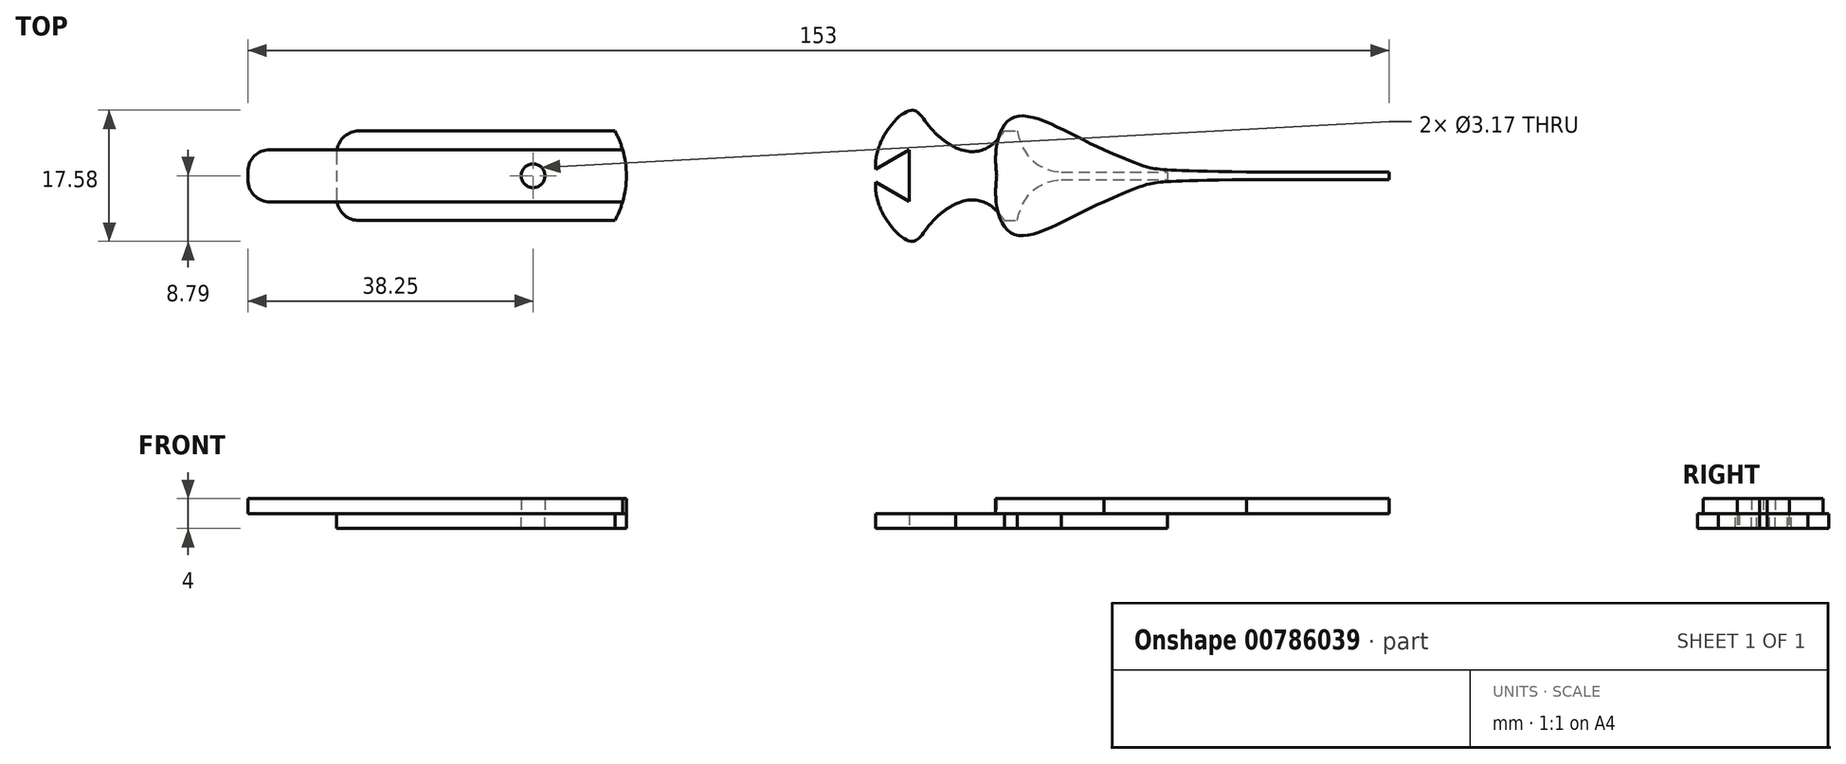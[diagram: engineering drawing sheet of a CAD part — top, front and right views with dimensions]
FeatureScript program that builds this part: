
annotation { "Feature Type Name" : "Feature", "Feature Type Description" : "" }
export const myFeature = defineFeature(function(context is Context, id is Id, definition is map)
    precondition{}
    {
        {
            var Q0;
            Q0=qCreatedBy(makeId("Top.planeOp"),FACE);
            var sketch = newSketch(context, id + "F0", { "sketchPlane" : qUnion([Q0])});
            skCircle(sketch, "E0", {"center": v(0, 0) * mm, "radius": 1.59 * mm});
            skLineSegment(sketch, "E1.bottom", {"start": v(-38.25, 3.5) * mm, "end": v(114.75, 3.5) * mm});
            skLineSegment(sketch, "E1.top", {"start": v(-38.25, -3.5) * mm, "end": v(114.75, -3.5) * mm});
            skLineSegment(sketch, "E1.left", {"start": v(-38.25, 3.5) * mm, "end": v(-38.25, -3.5) * mm});
            skLineSegment(sketch, "E1.right", {"start": v(114.75, 3.5) * mm, "end": v(114.75, -3.5) * mm});
            skCircle(sketch, "E2", {"center": v(0, 0) * mm, "radius": 12.5 * mm});
            skFitSpline(sketch, "E3", {"points": [v(76.5, -3.5) * mm, v(83.35, -0.96) * mm, v(95.63, -0.5) * mm], "startDerivative": vector(32.58, 14.52) * mm, "endDerivative": vector(48.68, 0.82) * mm});
            skFitSpline(sketch, "E4", {"points": [v(76.5, -3.5) * mm, v(64.47, -7.85) * mm, v(62.16, 0) * mm], "startDerivative": vector(-24.35, -10.45) * mm, "endDerivative": vector(3.38, 23.63) * mm});
            skLineSegment(sketch, "E5", {"start": v(0, 0) * mm, "end": v(229.5, 0) * mm, "construction": true});
            skLineSegment(sketch, "E6", {"start": v(95.63, -0.5) * mm, "end": v(114.75, -0.5) * mm});
            skFitSpline(sketch, "E7.MirrorCS", {"points": [v(76.5, 3.5) * mm, v(64.47, 7.85) * mm, v(62.16, 0) * mm], "startDerivative": vector(-24.35, 10.45) * mm, "endDerivative": vector(3.38, -23.63) * mm});
            skFitSpline(sketch, "E8.MirrorCS", {"points": [v(76.5, 3.5) * mm, v(83.35, 0.96) * mm, v(95.63, 0.5) * mm], "startDerivative": vector(32.58, -14.52) * mm, "endDerivative": vector(48.68, -0.82) * mm});
            skLineSegment(sketch, "E9.MirrorCS", {"start": v(95.63, 0.5) * mm, "end": v(114.75, 0.5) * mm});
            skSolve(sketch);
        }
        {
            var Q0;
            {var subQ0=sQuery(id+"F0.wireOp",EDGE,"E1.left");Q0=makeQuery(id+"F0.imprint","IMPRINT",FACE,{"disambiguationData":[TD([[makeQuery(id+"F0.imprint","IMPRINT",EDGE,{"derivedFrom":subQ0}),1.0]])]});}
            var Q1;
            {var subQ0=sQuery(id+"F0.wireOp",EDGE,"E2");var subQ1=sQuery(id+"F0.wireOp",EDGE,"E1.bottom");var subQ2=makeQuery(id+"F0.imprint","INTERSECT",VERTEX,{"disambiguationData":[OD(0.0)],"derivedFrom":[subQ1,subQ0]});Q1=makeQuery(id+"F0.imprint","IMPRINT",FACE,{"disambiguationData":[TD([[makeQuery(id+"F0.imprint","IMPRINT",EDGE,{"disambiguationData":[TD([[subQ2,-1.0]])],"derivedFrom":subQ1}),1.0]])]});}
            var Q2;
            {var subQ0=sQuery(id+"F0.wireOp",EDGE,"E7.MirrorCS");var subQ1=sQuery(id+"F0.wireOp",EDGE,"E1.bottom");var subQ3=makeQuery(id+"F0.imprint","INTERSECT",VERTEX,{"derivedFrom":[subQ1,subQ0]});Q2=makeQuery(id+"F0.imprint","IMPRINT",FACE,{"disambiguationData":[TD([[makeQuery(id+"F0.imprint","IMPRINT",EDGE,{"disambiguationData":[TD([[subQ3,-1.0]])],"derivedFrom":subQ1}),1.0]])]});}
            var Q3;
            {var subQ0=sQuery(id+"F0.wireOp",EDGE,"E2");var subQ1=sQuery(id+"F0.wireOp",EDGE,"E1.top");var subQ2=makeQuery(id+"F0.imprint","INTERSECT",VERTEX,{"disambiguationData":[OD(0.0)],"derivedFrom":[subQ1,subQ0]});Q3=makeQuery(id+"F0.imprint","IMPRINT",FACE,{"disambiguationData":[TD([[makeQuery(id+"F0.imprint","IMPRINT",EDGE,{"disambiguationData":[TD([[subQ2,-1.0]])],"derivedFrom":subQ1}),-1.0]])]});}
            var Q4;
            {var subQ0=sQuery(id+"F0.wireOp",EDGE,"E4");var subQ1=sQuery(id+"F0.wireOp",EDGE,"E1.top");var subQ3=makeQuery(id+"F0.imprint","INTERSECT",VERTEX,{"derivedFrom":[subQ1,subQ0]});Q4=makeQuery(id+"F0.imprint","IMPRINT",FACE,{"disambiguationData":[TD([[makeQuery(id+"F0.imprint","IMPRINT",EDGE,{"disambiguationData":[TD([[subQ3,-1.0]])],"derivedFrom":subQ1}),-1.0]])]});}
            var Q5;
            {var subQ5=sQuery(id+"F0.wireOp",EDGE,"E2");var subQ6=sQuery(id+"F0.wireOp",EDGE,"E1.bottom");var subQ7=makeQuery(id+"F0.imprint","INTERSECT",VERTEX,{"disambiguationData":[OD(1.0)],"derivedFrom":[subQ6,subQ5]});Q5=makeQuery(id+"F0.imprint","IMPRINT",FACE,{"disambiguationData":[TD([[makeQuery(id+"F0.imprint","IMPRINT",EDGE,{"disambiguationData":[TD([[subQ7,-1.0]])],"derivedFrom":subQ6}),-1.0]])]});}
            var Q6;
            Q6=makeQuery(id+"F0.imprint","IMPRINT",FACE,{"disambiguationData":[TD([[makeQuery(id+"F0.imprint","IMPRINT",EDGE,{"derivedFrom":sQuery(id+"F0.wireOp",EDGE,"E0")}),-1.0]])]});
            var Q7;
            {var subQ8=sQuery(id+"F0.wireOp",EDGE,"E3");Q7=makeQuery(id+"F0.imprint","IMPRINT",FACE,{"disambiguationData":[TD([[makeQuery(id+"F0.imprint","IMPRINT",EDGE,{"derivedFrom":subQ8}),1.0]])]});}
            extrude(context, id + "F1", {"entities" : qUnion([Q0, Q1, Q2, Q3, Q4, Q5, Q6, Q7]), "depth" : 2 * mm});
        }
        {
            var Q0;
            Q0=qCreatedBy(makeId("Top.planeOp"),FACE);
            var sketch = newSketch(context, id + "F2", { "sketchPlane" : qUnion([Q0])});
            skCircle(sketch, "E10", {"center": v(0, 0) * mm, "radius": 1.59 * mm});
            skLineSegment(sketch, "E11.bottom", {"start": v(-26.33, 6) * mm, "end": v(85, 6) * mm});
            skLineSegment(sketch, "E11.top", {"start": v(-26.33, -6) * mm, "end": v(85, -6) * mm});
            skLineSegment(sketch, "E11.left", {"start": v(-26.33, 6) * mm, "end": v(-26.33, -6) * mm});
            skLineSegment(sketch, "E11.right", {"start": v(85, 6) * mm, "end": v(85, -6) * mm});
            skCircle(sketch, "E12", {"center": v(0, 0) * mm, "radius": 12.5 * mm});
            skLineSegment(sketch, "E13.right", {"start": v(85, -12.54) * mm, "end": v(85, -19.22) * mm});
            skFitSpline(sketch, "E14", {"points": [v(56.67, -3.75) * mm, v(64.42, -7.88) * mm, v(70.83, -0.5) * mm], "startDerivative": vector(32.58, 14.52) * mm, "endDerivative": vector(38.81, 3.07) * mm});
            skFitSpline(sketch, "E15", {"points": [v(56.67, -3.75) * mm, v(50.67, -8.78) * mm, v(46.04, 0) * mm], "startDerivative": vector(-26.59, -13.5) * mm, "endDerivative": vector(5.2, 23.3) * mm});
            skLineSegment(sketch, "E16", {"start": v(0, 0) * mm, "end": v(229.5, 0) * mm, "construction": true});
            skLineSegment(sketch, "E17", {"start": v(70.83, -0.5) * mm, "end": v(85, -0.5) * mm});
            skFitSpline(sketch, "E18.MirrorCS", {"points": [v(56.67, 3.75) * mm, v(50.67, 8.78) * mm, v(46.04, 0) * mm], "startDerivative": vector(-26.59, 13.5) * mm, "endDerivative": vector(5.2, -23.3) * mm});
            skFitSpline(sketch, "E19.MirrorCS", {"points": [v(56.67, 3.75) * mm, v(64.42, 7.88) * mm, v(70.83, 0.5) * mm], "startDerivative": vector(32.58, -14.52) * mm, "endDerivative": vector(38.81, -3.07) * mm});
            skLineSegment(sketch, "E20.MirrorCS", {"start": v(70.83, 0.5) * mm, "end": v(85, 0.5) * mm});
            skSolve(sketch);
        }
        {
            var Q0;
            {var subQ0=sQuery(id+"F2.wireOp",EDGE,"E11.left");Q0=makeQuery(id+"F2.imprint","IMPRINT",FACE,{"disambiguationData":[TD([[makeQuery(id+"F2.imprint","IMPRINT",EDGE,{"derivedFrom":subQ0}),1.0]])]});}
            var Q1;
            {var subQ0=sQuery(id+"F2.wireOp",EDGE,"E12");var subQ1=sQuery(id+"F2.wireOp",EDGE,"E11.bottom");var subQ2=makeQuery(id+"F2.imprint","INTERSECT",VERTEX,{"disambiguationData":[OD(0.0)],"derivedFrom":[subQ1,subQ0]});Q1=makeQuery(id+"F2.imprint","IMPRINT",FACE,{"disambiguationData":[TD([[makeQuery(id+"F2.imprint","IMPRINT",EDGE,{"disambiguationData":[TD([[subQ2,-1.0]])],"derivedFrom":subQ1}),1.0]])]});}
            var Q2;
            {var subQ0=sQuery(id+"F2.wireOp",EDGE,"E12");var subQ1=sQuery(id+"F2.wireOp",EDGE,"E11.top");var subQ2=makeQuery(id+"F2.imprint","INTERSECT",VERTEX,{"disambiguationData":[OD(0.0)],"derivedFrom":[subQ1,subQ0]});Q2=makeQuery(id+"F2.imprint","IMPRINT",FACE,{"disambiguationData":[TD([[makeQuery(id+"F2.imprint","IMPRINT",EDGE,{"disambiguationData":[TD([[subQ2,-1.0]])],"derivedFrom":subQ1}),-1.0]])]});}
            var Q3;
            {var subQ0=sQuery(id+"F2.wireOp",EDGE,"E20.MirrorCS");var subQ1=sQuery(id+"F2.wireOp",EDGE,"E11.right");var subQ2=makeQuery(id+"F2.imprint","INTERSECT",VERTEX,{"derivedFrom":[subQ1,subQ0]});Q3=makeQuery(id+"F2.imprint","IMPRINT",FACE,{"disambiguationData":[TD([[makeQuery(id+"F2.imprint","IMPRINT",EDGE,{"disambiguationData":[TD([[subQ2,-1.0]])],"derivedFrom":subQ1}),1.0]])]});}
            var Q4;
            {var subQ5=sQuery(id+"F2.wireOp",EDGE,"E12");var subQ6=sQuery(id+"F2.wireOp",EDGE,"E11.bottom");var subQ7=makeQuery(id+"F2.imprint","INTERSECT",VERTEX,{"disambiguationData":[OD(1.0)],"derivedFrom":[subQ6,subQ5]});Q4=makeQuery(id+"F2.imprint","IMPRINT",FACE,{"disambiguationData":[TD([[makeQuery(id+"F2.imprint","IMPRINT",EDGE,{"disambiguationData":[TD([[subQ7,-1.0]])],"derivedFrom":subQ6}),-1.0]])]});}
            var Q5;
            Q5=makeQuery(id+"F2.imprint","IMPRINT",FACE,{"disambiguationData":[TD([[makeQuery(id+"F2.imprint","IMPRINT",EDGE,{"derivedFrom":sQuery(id+"F2.wireOp",EDGE,"E10")}),-1.0]])]});
            var Q6;
            {var subQ0=sQuery(id+"F2.wireOp",EDGE,"E17");Q6=makeQuery(id+"F2.imprint","IMPRINT",FACE,{"disambiguationData":[TD([[makeQuery(id+"F2.imprint","IMPRINT",EDGE,{"derivedFrom":subQ0}),1.0]])]});}
            var Q7;
            {var subQ0=sQuery(id+"F2.wireOp",EDGE,"E14");var subQ1=sQuery(id+"F2.wireOp",EDGE,"E11.top");var subQ2=makeQuery(id+"F2.imprint","INTERSECT",VERTEX,{"disambiguationData":[OD(0.0)],"derivedFrom":[subQ1,subQ0]});Q7=makeQuery(id+"F2.imprint","IMPRINT",FACE,{"disambiguationData":[TD([[makeQuery(id+"F2.imprint","IMPRINT",EDGE,{"disambiguationData":[TD([[subQ2,-1.0]])],"derivedFrom":subQ1}),-1.0]])]});}
            var Q8;
            {var subQ0=sQuery(id+"F2.wireOp",EDGE,"E19.MirrorCS");var subQ1=sQuery(id+"F2.wireOp",EDGE,"E11.bottom");var subQ2=makeQuery(id+"F2.imprint","INTERSECT",VERTEX,{"disambiguationData":[OD(0.0)],"derivedFrom":[subQ1,subQ0]});Q8=makeQuery(id+"F2.imprint","IMPRINT",FACE,{"disambiguationData":[TD([[makeQuery(id+"F2.imprint","IMPRINT",EDGE,{"disambiguationData":[TD([[subQ2,-1.0]])],"derivedFrom":subQ1}),1.0]])]});}
            var Q9;
            {var subQ0=sQuery(id+"F2.wireOp",EDGE,"E18.MirrorCS");var subQ1=sQuery(id+"F2.wireOp",EDGE,"E11.bottom");var subQ2=makeQuery(id+"F2.imprint","INTERSECT",VERTEX,{"disambiguationData":[OD(0.0)],"derivedFrom":[subQ1,subQ0]});Q9=makeQuery(id+"F2.imprint","IMPRINT",FACE,{"disambiguationData":[TD([[makeQuery(id+"F2.imprint","IMPRINT",EDGE,{"disambiguationData":[TD([[subQ2,-1.0]])],"derivedFrom":subQ1}),1.0]])]});}
            var Q10;
            {var subQ0=sQuery(id+"F2.wireOp",EDGE,"E15");var subQ1=sQuery(id+"F2.wireOp",EDGE,"E11.top");var subQ2=makeQuery(id+"F2.imprint","INTERSECT",VERTEX,{"disambiguationData":[OD(0.0)],"derivedFrom":[subQ1,subQ0]});Q10=makeQuery(id+"F2.imprint","IMPRINT",FACE,{"disambiguationData":[TD([[makeQuery(id+"F2.imprint","IMPRINT",EDGE,{"disambiguationData":[TD([[subQ2,-1.0]])],"derivedFrom":subQ1}),-1.0]])]});}
            extrude(context, id + "F3", {"entities" : qUnion([Q0, Q1, Q2, Q3, Q4, Q5, Q6, Q7, Q8, Q9, Q10]), "oppositeDirection" : true, "depth" : 2 * mm});
        }
        {
            var Q0;
            Q0=makeQuery(id+"F3.opExtrude","SWEPT_EDGE",EDGE,{"disambiguationData":[OSD([sQuery(id+"F2.wireOp",EDGE,"E11.bottom"),sQuery(id+"F2.wireOp",EDGE,"E11.left")])]});
            var Q1;
            Q1=makeQuery(id+"F3.opExtrude","SWEPT_EDGE",EDGE,{"disambiguationData":[OSD([sQuery(id+"F2.wireOp",EDGE,"E11.top"),sQuery(id+"F2.wireOp",EDGE,"E11.left")])]});
            var Q2;
            Q2=makeQuery(id+"F1.opExtrude","SWEPT_EDGE",EDGE,{"disambiguationData":[OSD([sQuery(id+"F0.wireOp",EDGE,"E1.bottom"),sQuery(id+"F0.wireOp",EDGE,"E1.left")])]});
            var Q3;
            Q3=makeQuery(id+"F1.opExtrude","SWEPT_EDGE",EDGE,{"disambiguationData":[OSD([sQuery(id+"F0.wireOp",EDGE,"E1.top"),sQuery(id+"F0.wireOp",EDGE,"E1.left")])]});
            fillet(context, id + "F4", {"entities" : qUnion([Q0, Q1, Q2, Q3]), "radius" : 3 * mm, "tangentPropagation" : true, "allowEdgeOverflow" : false});
        }
        {
            var Q0;
            Q0=makeQuery(id+"F3.opExtrude","CAP_FACE",FACE,{"disambiguationData":[OSD([sQuery(id+"F2.wireOp",EDGE,"E11.bottom"),sQuery(id+"F2.wireOp",EDGE,"E11.top"),sQuery(id+"F2.wireOp",EDGE,"E11.left"),sQuery(id+"F2.wireOp",EDGE,"E11.right"),sQuery(id+"F2.wireOp",EDGE,"E10"),sQuery(id+"F2.wireOp",EDGE,"E12"),sQuery(id+"F2.wireOp",EDGE,"E14"),sQuery(id+"F2.wireOp",EDGE,"E15"),sQuery(id+"F2.wireOp",EDGE,"E17"),sQuery(id+"F2.wireOp",EDGE,"E18.MirrorCS"),sQuery(id+"F2.wireOp",EDGE,"E19.MirrorCS"),sQuery(id+"F2.wireOp",EDGE,"E20.MirrorCS")])],"isStart":false});
            var sketch = newSketch(context, id + "F5", { "sketchPlane" : qUnion([Q0])});
            skLineSegment(sketch, "E21", {"start": v(-1.59, 0) * mm, "end": v(100.11, 0) * mm, "construction": true});
            skCircle(sketch, "E22.cCircle", {"center": v(48.41, 0) * mm, "radius": 2 * mm, "construction": true});
            skLineSegment(sketch, "E22.0", {"start": v(50.41, -3.46) * mm, "end": v(44.41, 0) * mm});
            skLineSegment(sketch, "E22.1", {"start": v(44.41, 0) * mm, "end": v(50.41, 3.46) * mm});
            skLineSegment(sketch, "E22.2", {"start": v(50.41, 3.46) * mm, "end": v(50.41, -3.46) * mm});
            skPoint(sketch, "E22.0.midPoint", {"position": v(47.41, -1.73) * mm});
            skCircle(sketch, "E23.cCircle", {"center": v(35.09, 0) * mm, "radius": 3 * mm, "construction": true});
            skLineSegment(sketch, "E23.0", {"start": v(38.8, 0) * mm, "end": v(36.23, -3.53) * mm});
            skLineSegment(sketch, "E23.1", {"start": v(36.23, -3.53) * mm, "end": v(32.09, -2.18) * mm});
            skLineSegment(sketch, "E23.2", {"start": v(32.09, -2.18) * mm, "end": v(32.09, 2.18) * mm});
            skLineSegment(sketch, "E23.3", {"start": v(32.09, 2.18) * mm, "end": v(36.23, 3.53) * mm});
            skLineSegment(sketch, "E23.4", {"start": v(36.23, 3.53) * mm, "end": v(38.8, 0) * mm});
            skPoint(sketch, "E23.0.midPoint", {"position": v(37.51, -1.76) * mm});
            skCircle(sketch, "E24.cCircle", {"center": v(20.34, 0) * mm, "radius": 2.5 * mm, "construction": true});
            skLineSegment(sketch, "E24.0", {"start": v(23.88, 0) * mm, "end": v(20.34, -3.54) * mm});
            skLineSegment(sketch, "E24.1", {"start": v(20.34, -3.54) * mm, "end": v(16.8, 0) * mm});
            skLineSegment(sketch, "E24.2", {"start": v(16.8, 0) * mm, "end": v(20.34, 3.54) * mm});
            skLineSegment(sketch, "E24.3", {"start": v(20.34, 3.54) * mm, "end": v(23.88, 0) * mm});
            skPoint(sketch, "E24.0.midPoint", {"position": v(22.11, -1.77) * mm});
            skSolve(sketch);
        }
        {
            var Q0;
            Q0=qSketchRegion(id+"F5",true);
            extrude(context, id + "F6", {"entities" : qUnion([Q0]), "operationType" : NewBodyOperationType.REMOVE, "oppositeDirection" : true, "depth" : 25 * mm, "offsetDistance" : 25 * mm});
        }
        {
            var Q0;
            Q0=makeQuery(id+"F3.opExtrude","CAP_FACE",FACE,{"disambiguationData":[OSD([sQuery(id+"F2.wireOp",EDGE,"E11.bottom"),sQuery(id+"F2.wireOp",EDGE,"E11.top"),sQuery(id+"F2.wireOp",EDGE,"E11.left"),sQuery(id+"F2.wireOp",EDGE,"E11.right"),sQuery(id+"F2.wireOp",EDGE,"E10"),sQuery(id+"F2.wireOp",EDGE,"E12"),sQuery(id+"F2.wireOp",EDGE,"E14"),sQuery(id+"F2.wireOp",EDGE,"E15"),sQuery(id+"F2.wireOp",EDGE,"E17"),sQuery(id+"F2.wireOp",EDGE,"E18.MirrorCS"),sQuery(id+"F2.wireOp",EDGE,"E19.MirrorCS"),sQuery(id+"F2.wireOp",EDGE,"E20.MirrorCS")])],"isStart":false});
            var sketch = newSketch(context, id + "F7", { "sketchPlane" : qUnion([Q0])});
            skCircle(sketch, "E25", {"center": v(0, 8) * mm, "radius": 1.5 * mm});
            skLineSegment(sketch, "E26", {"start": v(-11.48, 0) * mm, "end": v(10.1, 0) * mm, "construction": true});
            skCircle(sketch, "E27.MirrorC", {"center": v(0, -8) * mm, "radius": 1.5 * mm});
            skSolve(sketch);
        }
        {
            var Q0;
            Q0=qSketchRegion(id+"F7",true);
            extrude(context, id + "F8", {"entities" : qUnion([Q0]), "operationType" : NewBodyOperationType.REMOVE, "oppositeDirection" : true, "depth" : 25 * mm, "offsetDistance" : 25 * mm});
        }
    });
